# Revit family: Plumbing-Urinals-Sloan-Valve-WES-1000
name_source: partatom
category: Plumbing Fixtures
units: mm (PartAtom-declared; Revit-internal decimal feet)

## family parameters
Cut with Voids When Loaded = No
Host = Face
OmniClass Number = 23.45.05.21.11.21
OmniClass Title = Urinals
Part Type = Normal
Room Calculation Point = No
Round Connector Dimension = Use Diameter
Shared = No

## types (2) — shared parameters
Assembly Code = D2010
CW Connection = No
Depth = 14.38 "
Edition number = 1
HW Connection = No
Height = 26.25 "
Keynote = 15410
Manufacturer = Sloan Valve
Product data url = https://www.bimobject.com
Sanitary Drain Connection Diameter = 2"
URL = www.sloanvalve.com
Vent Connection = No
WFU = 5
Width = 19.25 "
zero-valued in all types: CWFU, Default Elevation, HWFU

## per-type parameters (varying)
| type | Description | Part Number | Product Material | Waste Connection |
| WES-1000-STG | Vitreous China Waterfree Urinal with SloanTec® Glaze. | 1071000 | Sloan Valve - Vitreous China - SloanTec Glaze White | No |
| WES-1000 | Vitreous China Waterfree Urinal | 1001000 | Sloan Valve - Vitreous China - White | Yes |

note: column(s) folded — value = type name in every type: Model

## geometry (parser evidence)
native form markers: Sweep x4
no freeform markers — native parametric forms only
